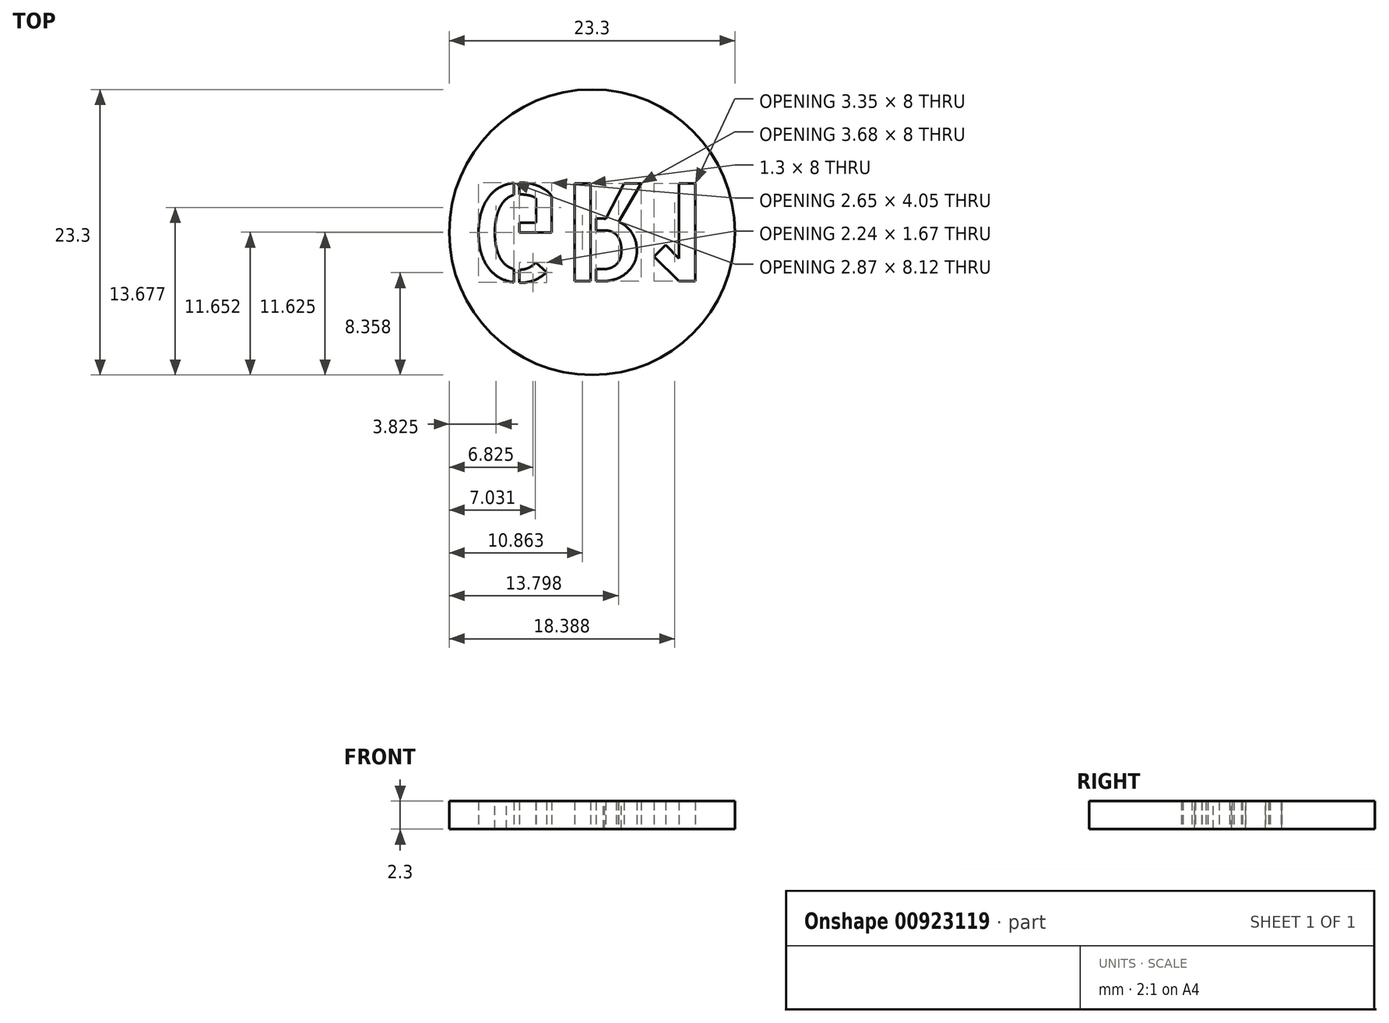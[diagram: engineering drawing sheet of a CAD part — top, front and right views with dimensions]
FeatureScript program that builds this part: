
annotation { "Feature Type Name" : "Feature", "Feature Type Description" : "" }
export const myFeature = defineFeature(function(context is Context, id is Id, definition is map)
    precondition{}
    {
        {
            var Q0;
            Q0=qCreatedBy(makeId("Top.planeOp"),FACE);
            var sketch = newSketch(context, id + "F0", { "sketchPlane" : qUnion([Q0])});
            skCircle(sketch, "E0", {"center": v(0, 0) * mm, "radius": 11.65 * mm});
            skSolve(sketch);
        }
        {
            var Q0;
            Q0=makeQuery(id+"F0.imprint","IMPRINT",FACE,{"disambiguationData":[TD([[makeQuery(id+"F0.imprint","IMPRINT",EDGE,{"derivedFrom":sQuery(id+"F0.wireOp",EDGE,"E0")}),1.0]])]});
            extrude(context, id + "F1", {"entities" : qUnion([Q0]), "depth" : 2.3 * mm, "offsetDistance" : 25 * mm});
        }
        {
            var Q0;
            Q0=makeQuery(id+"F1.opExtrude","CAP_FACE",FACE,{"disambiguationData":[OSD([sQuery(id+"F0.wireOp",EDGE,"E0")])],"isStart":true});
            var sketch = newSketch(context, id + "F2", { "sketchPlane" : qUnion([Q0])});
            skLineSegment(sketch, "E1.bottom", {"start": v(0, 0) * mm, "end": v(-10.52, 0) * mm});
            skLineSegment(sketch, "E1.top", {"start": v(0, 5) * mm, "end": v(-10.52, 5) * mm});
            skLineSegment(sketch, "E1.left", {"start": v(0, 0) * mm, "end": v(0, 5) * mm});
            skLineSegment(sketch, "E1.right", {"start": v(-10.52, 0) * mm, "end": v(-10.52, 5) * mm});
            skLineSegment(sketch, "E2.MirrorCS", {"start": v(0, 5) * mm, "end": v(10.52, 5) * mm});
            skLineSegment(sketch, "E3.MirrorCS", {"start": v(10.52, 0) * mm, "end": v(10.52, 5) * mm});
            skLineSegment(sketch, "E4.MirrorCS", {"start": v(-10.52, 0) * mm, "end": v(-10.52, -5) * mm});
            skLineSegment(sketch, "E5.MirrorCS", {"start": v(0, -5) * mm, "end": v(-10.52, -5) * mm});
            skLineSegment(sketch, "E6.MirrorCS", {"start": v(0, -5) * mm, "end": v(10.52, -5) * mm});
            skLineSegment(sketch, "E7.MirrorCS", {"start": v(10.52, 0) * mm, "end": v(10.52, -5) * mm});
            skText(sketch, "E8", { "text": "GR1", "fontName": "AllertaStencil-Regular.ttf"});
            const initialGuessF2  = {"E8": [-0.01012, -0.004, 1, 0, 0.008]};
            skSetInitialGuess(sketch, initialGuessF2);
            skSolve(sketch);
        }
        {
            var Q0;
            {var subQ6=sQuery(id+"F2.wireOp",EDGE,"E8.sketch_text.stroke-8");Q0=makeQuery(id+"F2.imprint","IMPRINT",FACE,{"disambiguationData":[TD([[makeQuery(id+"F2.imprint","IMPRINT",EDGE,{"derivedFrom":subQ6}),-1.0]])]});}
            var Q1;
            Q1=makeQuery(id+"F2.imprint","IMPRINT",FACE,{"disambiguationData":[TD([[makeQuery(id+"F2.imprint","IMPRINT",EDGE,{"derivedFrom":sQuery(id+"F2.wireOp",EDGE,"E8.sketch_text.stroke-0")}),-1.0]])]});
            var Q2;
            {var subQ0=sQuery(id+"F2.wireOp",EDGE,"E8.sketch_text.stroke-18");Q2=makeQuery(id+"F2.imprint","IMPRINT",FACE,{"disambiguationData":[TD([[makeQuery(id+"F2.imprint","IMPRINT",EDGE,{"derivedFrom":subQ0}),-1.0]])]});}
            var Q3;
            {var subQ5=sQuery(id+"F2.wireOp",EDGE,"E8.sketch_text.stroke-27");Q3=makeQuery(id+"F2.imprint","IMPRINT",FACE,{"disambiguationData":[TD([[makeQuery(id+"F2.imprint","IMPRINT",EDGE,{"derivedFrom":subQ5}),-1.0]])]});}
            var Q4;
            {var subQ5=sQuery(id+"F2.wireOp",EDGE,"E8.sketch_text.stroke-43");Q4=makeQuery(id+"F2.imprint","IMPRINT",FACE,{"disambiguationData":[TD([[makeQuery(id+"F2.imprint","IMPRINT",EDGE,{"derivedFrom":subQ5}),-1.0]])]});}
            var Q5;
            {var subQ5=sQuery(id+"F2.wireOp",EDGE,"E8.sketch_text.stroke-41");Q5=makeQuery(id+"F2.imprint","IMPRINT",FACE,{"disambiguationData":[TD([[makeQuery(id+"F2.imprint","IMPRINT",EDGE,{"derivedFrom":subQ5}),-1.0]])]});}
            var Q6;
            Q6=makeQuery(id+"F2.imprint","IMPRINT",FACE,{"disambiguationData":[TD([[makeQuery(id+"F2.imprint","IMPRINT",EDGE,{"derivedFrom":sQuery(id+"F2.wireOp",EDGE,"E8.sketch_text.stroke-45")}),-1.0]])]});
            var Q7;
            Q7=makeQuery(id+"F2.imprint","IMPRINT",FACE,{"disambiguationData":[TD([[makeQuery(id+"F2.imprint","IMPRINT",EDGE,{"derivedFrom":sQuery(id+"F2.wireOp",EDGE,"E8.sketch_text.stroke-71")}),-1.0]])]});
            extrude(context, id + "F3", {"entities" : qUnion([Q0, Q1, Q2, Q3, Q4, Q5, Q6, Q7]), "operationType" : NewBodyOperationType.REMOVE, "oppositeDirection" : true, "depth" : 25 * mm, "offsetDistance" : 25 * mm});
        }
    });
